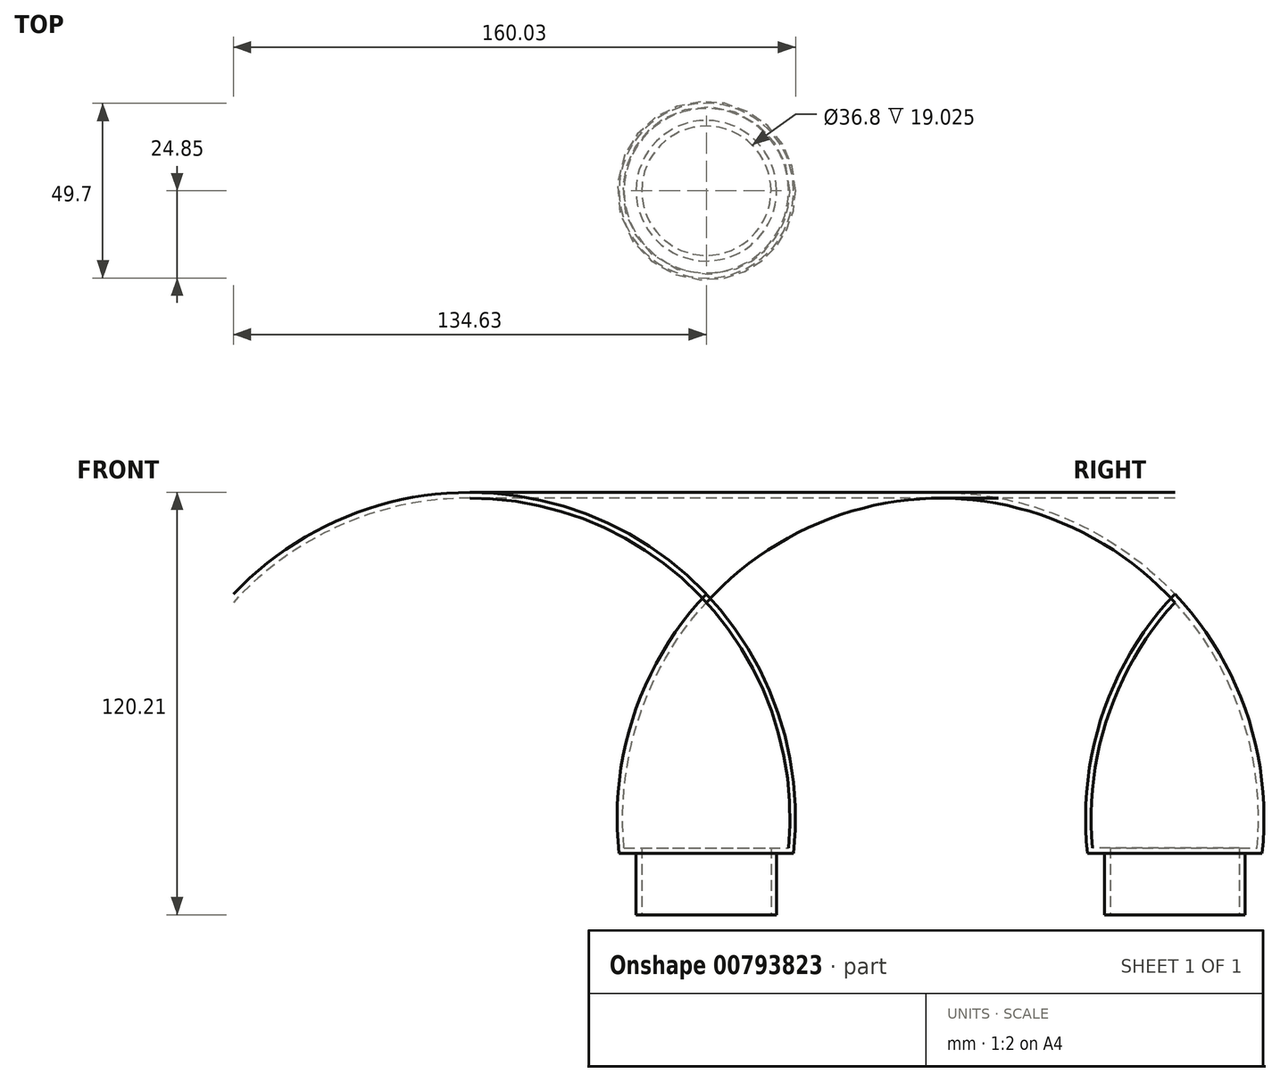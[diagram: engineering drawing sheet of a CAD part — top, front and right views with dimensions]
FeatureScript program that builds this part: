
annotation { "Feature Type Name" : "Feature", "Feature Type Description" : "" }
export const myFeature = defineFeature(function(context is Context, id is Id, definition is map)
    precondition{}
    {
        {
            var Q0;
            Q0=qCreatedBy(makeId("Front.planeOp"),FACE);
            var sketch = newSketch(context, id + "F0", { "sketchPlane" : qUnion([Q0])});
            skLineSegment(sketch, "E0", {"start": v(0, 0) * mm, "end": v(0, 88.9) * mm});
            skLineSegment(sketch, "E1", {"start": v(0, 0) * mm, "end": v(18.4, 0) * mm});
            skLineSegment(sketch, "E2", {"start": v(18.4, 0) * mm, "end": v(18.4, 19.03) * mm});
            skLineSegment(sketch, "E3", {"start": v(18.4, 19.03) * mm, "end": v(23.4, 19.03) * mm});
            skArc(sketch, "E4", {"start": v(23.4, 19.03) * mm, "mid": v(19.08, 56.43) * mm, "end": v(0, 88.9) * mm});
            skArc(sketch, "E5.0", {"start": v(24.85, 17.43) * mm, "mid": v(20.55, 57.07) * mm, "end": v(0, 91.25) * mm});
            skLineSegment(sketch, "E5.1", {"start": v(20, 17.43) * mm, "end": v(24.85, 17.43) * mm});
            skLineSegment(sketch, "E5.2", {"start": v(20, 0) * mm, "end": v(20, 17.43) * mm});
            skLineSegment(sketch, "E6", {"start": v(18.4, 0) * mm, "end": v(20, 0) * mm});
            skLineSegment(sketch, "E7", {"start": v(0, 88.9) * mm, "end": v(0, 91.25) * mm});
            skSolve(sketch);
        }
        {
            var Q0;
            Q0=makeQuery(id+"F0.imprint","IMPRINT",FACE,{"disambiguationData":[TD([[makeQuery(id+"F0.imprint","IMPRINT",EDGE,{"derivedFrom":sQuery(id+"F0.wireOp",EDGE,"E2")}),-1.0]])]});
            var Q1;
            Q1=sQuery(id+"F0.wireOp",EDGE,"E0");
            revolve(context, id + "F1", {"surfaceOperationType" : NewSurfaceOperationType.NEW, "entities" : qUnion([Q0]), "axis" : qUnion([Q1]), "revolveType" : RevolveType.FULL});
        }
    });
